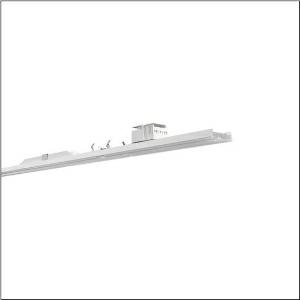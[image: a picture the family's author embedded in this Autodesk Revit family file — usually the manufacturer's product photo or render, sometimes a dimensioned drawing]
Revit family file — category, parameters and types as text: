
# Revit family: licross_r__11_recessed_mo_51tl18vn555f_c182
name_source: partatom
category: Lighting Fixtures
units: mm (PartAtom-declared; Revit-internal decimal feet)

## family parameters
Cut with Voids When Loaded = No
Host = Face
Light Source = No
Part Type = Normal
Room Calculation Point = No
Round Connector Dimension = Use Diameter
Shared = No

## types (1)
- --- (1 x LED, 5570 lm, 33.6 W, 5000K)
    Apparent Load = 34 VA
    CIE Flux Codes = 83 96 99 100 100
    Color Rendering = 80
    Color Temperature = 5000K
    Default Elevation = 1800 mm
    Description = Licross® 11 Recessed MOluminaire insert, length: 1.500mm, width: 66mm, height: 67mm, LED rated luminous flux: 5.570lm, light colour: 850, control gear: DALI 2, CLO, control gear: ECG DALI, with plug, 5-pole, with phase selection, mains connection: 220..240V, AC, 50/60Hz, halogen-free wiring, primary optical cover: cover, of PMMA, light emission: direct distribution, protection rating (complete): IP40, insulation class (complete): insulation class I (protective earthing), certification: CE, ENEC, VDE, UKCA, protection symbol: D if used in an environment without relevant dust loads with corresponding accessories, permissible ambient temperature for indoor applications: -25..+45°C, corresponds to IFS (International Featured Standards) requirements for safety and quality in the food industry, reducing of maximum allowable ambient temperature of 5°C with ceiling mounting, packaging unit: 1 piece
    Height = 58 mm
    Lamp = 1 x LED
    Lamp Light Flux = 5570 lm
    Lamp Power = 33.6 W
    Lamp count = 1
    Length = 1500 mm
    Luminous efficacy = 166 lm/W
    Manufacturer = Siteco
    ModVariant = No
    Model = 51TL18VN555F
    Mounting Place = Ceiling
    Mounting Type = Pendant
    Number of Poles = 1
    OnlyDefault = Yes
    Power Factor = 1
    Product Name = Licross® 11 Recessed MO
    Product group = luminaire insert
    ProductGroupID = 902
    Protection Class = Protection class I
    Protection Degree = IP 40
    RLX_Detail_Level = 1
    RlxData = <blob elided: 22385 chars, md5=50620915>
    Socket = socket
    Standby Power = 0 W
    System Light Flux = 5570 lm
    System Power = 34 W
    Type Comments = factory setting: luminous flux: 100 % | dim-lin: 254 | 221 mA
    Type Image = l_1266722.jpg
    URL = http://relux.com
    VarID = @adj_128903
    Voltage = 0 V
    Weight = 0.00 kg
    Width = 66 mm

## geometry (parser evidence)
native form markers: Blend x4, Sweep x10
no freeform markers — native parametric forms only
